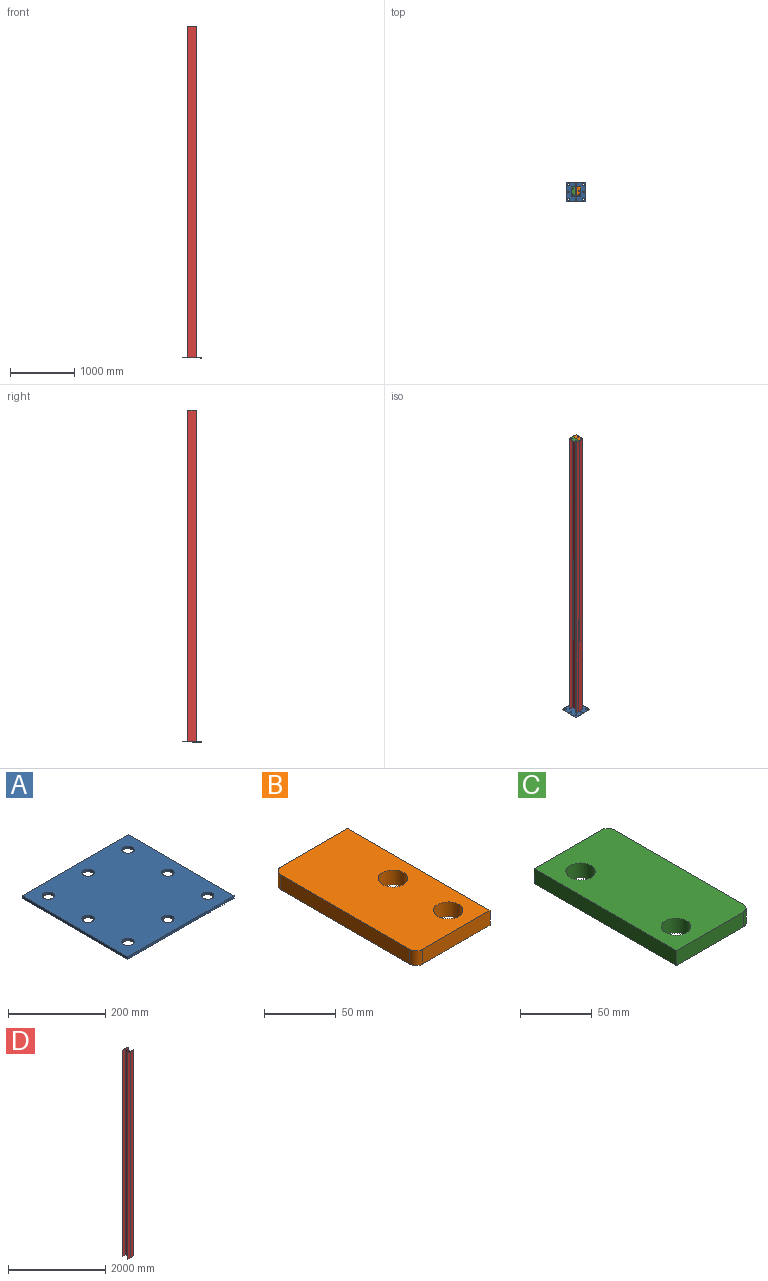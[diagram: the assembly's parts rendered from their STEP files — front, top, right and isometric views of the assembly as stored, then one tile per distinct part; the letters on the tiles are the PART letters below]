
ASSEMBLY  parts=4 mates=1
PART A: 14 faces, bbox 308.2x308.2x6.4 mm
  f0: plane 308.22x308.22mm, normal (0,0,1), area 90943.6mm2, adj f1,f3,f4,f5,f6,f7,f8,f9
  f1: plane 308.22x6.35mm, normal (-1,0,0), area 1957.2mm2, adj f0,f2,f3,f4
  f2: plane 308.22x308.22mm, normal (0,0,-1), area 90943.6mm2, adj f1,f3,f4,f5,f6,f7,f8,f9
  f3: plane 308.22x6.35mm, normal (0,-1,0), area 1957.2mm2, adj f0,f1,f2,f5
  f4: plane 308.22x6.35mm, normal (0,1,0), area 1957.2mm2, adj f0,f1,f2,f5
  f5: plane 308.22x6.35mm, normal (1,0,0), area 1957.2mm2, adj f0,f2,f3,f4
  f6: cylinder r=12.7mm len=25.4mm, axis (0,0,-1), area 506.7mm2, adj f0,f2
  f7: cylinder r=12.7mm len=25.4mm, axis (0,0,-1), area 506.7mm2, adj f0,f2
  f8: cylinder r=12.7mm len=25.4mm, axis (0,0,-1), area 506.7mm2, adj f0,f2
  f9: cylinder r=12.7mm len=25.4mm, axis (0,0,-1), area 506.7mm2, adj f0,f2
  f10: cylinder r=12.7mm len=25.4mm, axis (0,0,-1), area 506.7mm2, adj f0,f2
  f11: cylinder r=12.7mm len=25.4mm, axis (0,0,-1), area 506.7mm2, adj f0,f2
  f12: cylinder r=12.7mm len=25.4mm, axis (0,0,-1), area 506.7mm2, adj f0,f2
  f13: cylinder r=12.7mm len=25.4mm, axis (0,0,-1), area 506.7mm2, adj f0,f2
PART B: 10 faces, bbox 72.8x140.5x12.7 mm
  f0: cylinder r=6.35mm len=12.7mm, axis (0,0,-1), area 126.7mm2, adj f2,f3,f4,f7
  f1: cylinder r=6.35mm len=12.7mm, axis (0,0,-1), area 126.7mm2, adj f2,f3,f4,f6
  f2: plane 127.76x12.7mm, normal (-1,0,0), area 1622.6mm2, adj f0,f1,f3,f4
  f3: plane 140.46x72.77mm, normal (0,0,-1), area 9536.1mm2, adj f0,f1,f2,f5,f6,f7,f8,f9
  f4: plane 140.46x72.77mm, normal (0,0,1), area 9536.1mm2, adj f0,f1,f2,f5,f6,f7,f8,f9
  f5: plane 140.46x12.7mm, normal (1,0,0), area 1783.9mm2, adj f3,f4,f6,f7
  f6: plane 66.42x12.7mm, normal (0,1,0), area 843.6mm2, adj f1,f3,f4,f5
  f7: plane 66.42x12.7mm, normal (0,-1,0), area 843.6mm2, adj f0,f3,f4,f5
  f8: cylinder r=10.31mm len=20.63mm, axis (0,0,1), area 822.9mm2, adj f3,f4
  f9: cylinder r=10.31mm len=20.63mm, axis (0,0,1), area 822.9mm2, adj f3,f4
PART C: 10 faces, bbox 72.8x140.5x12.7 mm
  f0: cylinder r=6.35mm len=12.7mm, axis (0,0,-1), area 126.7mm2, adj f2,f3,f4,f7
  f1: cylinder r=6.35mm len=12.7mm, axis (0,0,-1), area 126.7mm2, adj f2,f3,f4,f6
  f2: plane 127.76x12.7mm, normal (1,0,0), area 1622.6mm2, adj f0,f1,f3,f4
  f3: plane 140.46x72.77mm, normal (0,0,-1), area 9536.1mm2, adj f0,f1,f2,f5,f6,f7,f8,f9
  f4: plane 140.46x72.77mm, normal (0,0,1), area 9536.1mm2, adj f0,f1,f2,f5,f6,f7,f8,f9
  f5: plane 140.46x12.7mm, normal (-1,0,0), area 1783.9mm2, adj f3,f4,f6,f7
  f6: plane 66.42x12.7mm, normal (0,1,0), area 843.6mm2, adj f1,f3,f4,f5
  f7: plane 66.42x12.7mm, normal (0,-1,0), area 843.6mm2, adj f0,f3,f4,f5
  f8: cylinder r=10.31mm len=20.63mm, axis (0,0,1), area 822.9mm2, adj f3,f4
  f9: cylinder r=10.31mm len=20.63mm, axis (0,0,1), area 822.9mm2, adj f3,f4
PART D: 18 faces, bbox 152.1x152.1x5177.5 mm
  f0: plane 152.15x152.15mm, normal (0,0,1), area 2739.9mm2, adj f2,f3,f4,f5,f6,f7,f8,f9
  f1: plane 152.15x152.15mm, normal (0,0,-1), area 2739.9mm2, adj f2,f3,f4,f5,f6,f7,f8,f9
  f2: cylinder r=6.35mm len=5177.54mm, axis (0,0,-1), area 51644.3mm2, adj f0,f1,f3,f17
  f3: plane 5177.54x127.76mm, normal (-1,0,0), area 661492.4mm2, adj f0,f1,f2,f4
  f4: cylinder r=6.35mm len=5177.54mm, axis (0,0,-1), area 51644.3mm2, adj f0,f1,f3,f5
  f5: plane 5177.54x66.42mm, normal (0,-1,0), area 343897.1mm2, adj f0,f1,f4,f6
  f6: plane 5177.54x5.84mm, normal (-1,0,0), area 30247.2mm2, adj f0,f1,f5,f7
  f7: plane 5177.54x152.15mm, normal (0,1,0), area 787741.4mm2, adj f0,f1,f6,f8
  f8: plane 5177.54x5.84mm, normal (1,0,0), area 30247.2mm2, adj f0,f1,f7,f9
  f9: plane 5177.54x66.42mm, normal (0,-1,0), area 343897.1mm2, adj f0,f1,f8,f10
  f10: cylinder r=6.35mm len=5177.54mm, axis (0,0,-1), area 51644.3mm2, adj f0,f1,f9,f11
  f11: plane 5177.54x127.76mm, normal (1,0,0), area 661492.4mm2, adj f0,f1,f10,f12
  f12: cylinder r=6.35mm len=5177.54mm, axis (0,0,-1), area 51644.3mm2, adj f0,f1,f11,f13
  f13: plane 5177.54x66.42mm, normal (0,1,0), area 343897.1mm2, adj f0,f1,f12,f14
  f14: plane 5177.54x5.84mm, normal (1,0,0), area 30247.2mm2, adj f0,f1,f13,f15
  f15: plane 5177.54x152.15mm, normal (0,-1,0), area 787741.4mm2, adj f0,f1,f14,f16
  f16: plane 5177.54x5.84mm, normal (-1,0,0), area 30247.2mm2, adj f0,f1,f15,f17
  f17: plane 5177.54x66.42mm, normal (0,1,0), area 343897.1mm2, adj f0,f1,f2,f16
PLACE A t=(-2586.95,-5601.78,2965.38)mm
PLACE B at identity
PLACE C at identity
PLACE D at identity fixed
MATE fastened A.f0 <-> D.f1  axis (0,0,1) through (-5867.53,-2362.33,-5177.54)mm
